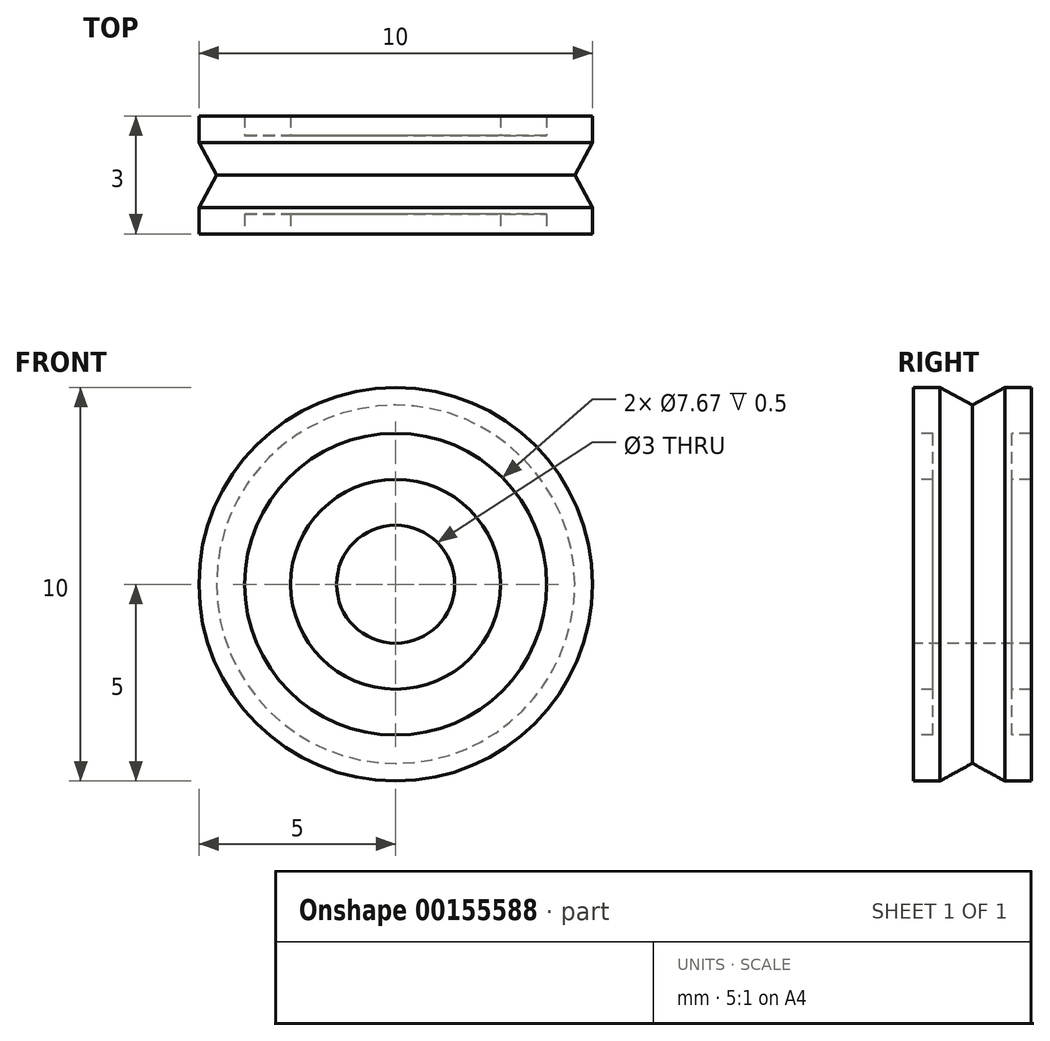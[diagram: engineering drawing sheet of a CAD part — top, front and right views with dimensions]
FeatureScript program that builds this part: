
annotation { "Feature Type Name" : "Feature", "Feature Type Description" : "" }
export const myFeature = defineFeature(function(context is Context, id is Id, definition is map)
    precondition{}
    {
        {
            var Q0;
            Q0=qCreatedBy(makeId("Right.planeOp"),FACE);
            var sketch = newSketch(context, id + "F0", { "sketchPlane" : qUnion([Q0])});
            skLineSegment(sketch, "E0", {"start": v(0, 1.5) * mm, "end": v(0, 5) * mm});
            skLineSegment(sketch, "E1", {"start": v(0, 5) * mm, "end": v(0.67, 5) * mm});
            skLineSegment(sketch, "E2", {"start": v(0.67, 5) * mm, "end": v(1.5, 4.55) * mm});
            skLineSegment(sketch, "E3", {"start": v(1.5, 4.55) * mm, "end": v(2.32, 5) * mm});
            skLineSegment(sketch, "E4", {"start": v(2.32, 5) * mm, "end": v(3, 5) * mm});
            skLineSegment(sketch, "E5", {"start": v(3, 5) * mm, "end": v(3, 1.5) * mm});
            skLineSegment(sketch, "E6", {"start": v(3, 1.5) * mm, "end": v(0, 1.5) * mm});
            skLineSegment(sketch, "E7", {"start": v(0, 0) * mm, "end": v(3, 0) * mm});
            skLineSegment(sketch, "E8", {"start": v(0, 2.67) * mm, "end": v(0.5, 2.67) * mm});
            skLineSegment(sketch, "E9", {"start": v(0.5, 2.67) * mm, "end": v(0.5, 3.83) * mm});
            skLineSegment(sketch, "E10", {"start": v(0.5, 3.83) * mm, "end": v(0, 3.83) * mm});
            skLineSegment(sketch, "E11", {"start": v(3, 2.67) * mm, "end": v(2.5, 2.67) * mm});
            skLineSegment(sketch, "E12", {"start": v(2.5, 2.67) * mm, "end": v(2.5, 3.83) * mm});
            skLineSegment(sketch, "E13", {"start": v(2.5, 3.83) * mm, "end": v(3, 3.83) * mm});
            skSolve(sketch);
        }
        {
            var Q0;
            Q0=makeQuery(id+"F0.imprint","IMPRINT",FACE,{"disambiguationData":[TD([[makeQuery(id+"F0.imprint","IMPRINT",EDGE,{"derivedFrom":sQuery(id+"F0.wireOp",EDGE,"E0")}),-1.0]])]});
            var Q1;
            Q1=sQuery(id+"F0.wireOp",EDGE,"E7");
            revolve(context, id + "F1", {"entities" : qUnion([Q0]), "axis" : qUnion([Q1]), "revolveType" : RevolveType.FULL});
        }
    });
